# Revit family: Atlas_Sound_AH94-12T-BSG
name_source: partatom
category: Communication Devices
units: mm (PartAtom-declared; Revit-internal decimal feet)

## family parameters
Always vertical = No
Cut with Voids When Loaded = No
Maintain Annotation Orientation = No
Part Type = Normal
Room Calculation Point = No
Round Connector Dimension = Use Diameter
Shared = No
Work Plane-Based = Yes

## types (1)
- Full-Range, Outdoor, Horn Loudspeaker
    100V Taps = 7.5, 15, 30, & 60 watts
    70V Taps = 7.5, 15, 30, & 60 watts
    Baffle Material = <By Category>
    Body Material = Default
    Color = <By Category>
    Cost = 1433.99 $
    Cost MSRP = 1433.99 $
    Coverage Horizontal = 90.00°
    Coverage Vertical = 0.00°
    Default Elevation = 48 "
    Depth = 22.57 "
    Description = 12" 2-WAY STADIUM HORN LOUDSPEAKER SYSTEM 90° X 40°
    Dispersion Angle = 90.00°
    Enclosure Material = <By Category>
    Family Code (default) = LOUD SPEAKERS
    Frequency Response  = 80Hz - 15kHz (±5dB)
    Grill Material = QF_Plastic - Black - Fine Textured
    HF Driver = 90° H x 40°V HF horn
    Height = 24.68 "
    IQ Category = SPEAKERS
    Impedance = 8
    Ingress Protection = IP45 When Tilted 5° Downwards
    Input Connectors = Barrier Terminal
    Manufacturer = ATLAS SOUND
    Manufacturer URL = https://www.atlasied.com
    Market = Commercial, Higher Education, Emergency
    MasterFormat = 27 41 13
    MaterFormat Title = SPEAKERS
    Maximum Output = 126dB (Rated Power @ 1M)
    Model = AH94-12T-BSG
    Mount Material = Default
    OmniClass Number = 23-37 17 13 19
    OmniClass Title = SPEAKERS
    Pitch = 0.00°
    Power Rating (RMS) = 200 watts
    Product Documentation Link = https://www.atlasied.com
    Product Page URL = https://www.atlasied.com
    Rotation = 0.00°
    SPL Max = 107
    ScheduleType |RF| = AtlasIED Master
    Sensitivity = 103
    Speaker Dispersion = 90.00°
    Transformer Option = Yes
    URL = www.atlassound.com
    Vertical Symmetry = Yes
    Warranty = 5 Year
    Weight Product = 85
    Width = 22.06 "

## geometry (parser evidence)
native form markers: Blend x10, Sweep x6
no freeform markers — native parametric forms only
